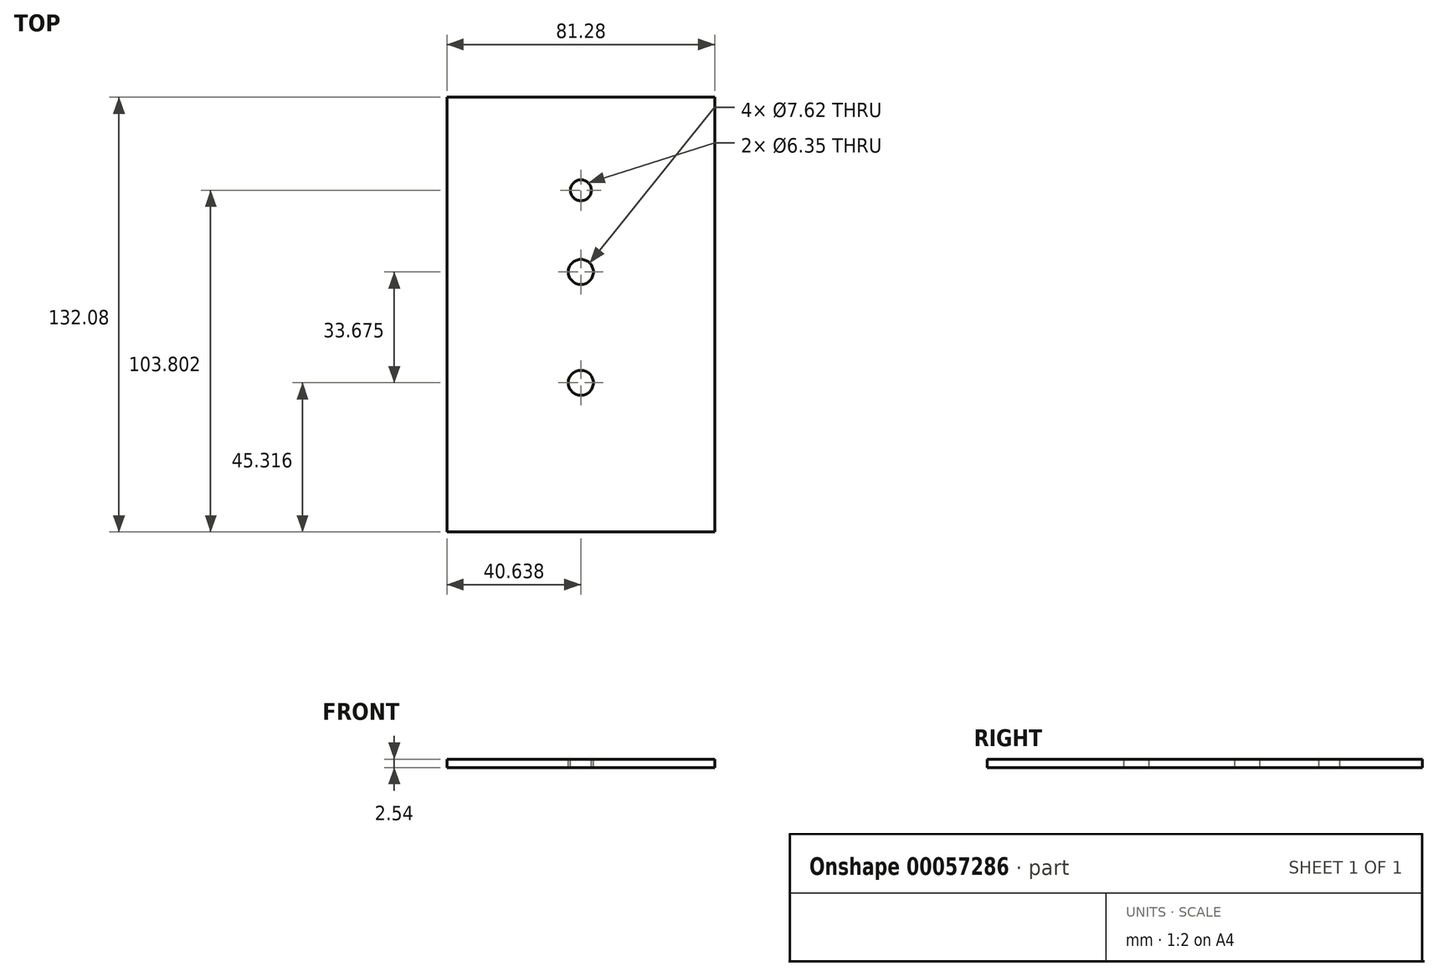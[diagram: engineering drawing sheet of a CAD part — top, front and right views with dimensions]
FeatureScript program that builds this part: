
annotation { "Feature Type Name" : "Feature", "Feature Type Description" : "" }
export const myFeature = defineFeature(function(context is Context, id is Id, definition is map)
    precondition{}
    {
        {
            var Q0;
            Q0=qCreatedBy(makeId("Top.planeOp"),FACE);
            var sketch = newSketch(context, id + "F0", { "sketchPlane" : qUnion([Q0])});
            skLineSegment(sketch, "E0.bottom", {"start": v(-159.06, -69.05) * mm, "end": v(-77.78, -69.05) * mm});
            skLineSegment(sketch, "E0.top", {"start": v(-159.06, 63.03) * mm, "end": v(-77.78, 63.03) * mm});
            skLineSegment(sketch, "E0.left", {"start": v(-159.06, -69.05) * mm, "end": v(-159.06, 63.03) * mm});
            skLineSegment(sketch, "E0.right", {"start": v(-77.78, -69.05) * mm, "end": v(-77.78, 63.03) * mm});
            skSolve(sketch);
        }
        {
            var Q0;
            Q0=makeQuery(id+"F0.imprint","IMPRINT",FACE,{"disambiguationData":[TD([[makeQuery(id+"F0.imprint","IMPRINT",EDGE,{"derivedFrom":sQuery(id+"F0.wireOp",EDGE,"E0.bottom")}),1.0]])]});
            extrude(context, id + "F1", {"entities" : qUnion([Q0]), "depth" : 2.54 * mm});
        }
        {
            var Q0;
            Q0=makeQuery(id+"F1.opExtrude","CAP_FACE",FACE,{"disambiguationData":[OSD([sQuery(id+"F0.wireOp",EDGE,"E0.bottom"),sQuery(id+"F0.wireOp",EDGE,"E0.top"),sQuery(id+"F0.wireOp",EDGE,"E0.left"),sQuery(id+"F0.wireOp",EDGE,"E0.right")])],"isStart":false});
            var sketch = newSketch(context, id + "F2", { "sketchPlane" : qUnion([Q0])});
            skCircle(sketch, "E1", {"center": v(-118.42, 34.75) * mm, "radius": 3.18 * mm});
            skSolve(sketch);
        }
        {
            var Q0;
            Q0=makeQuery(id+"F2.imprint","IMPRINT",FACE,{"disambiguationData":[TD([[makeQuery(id+"F2.imprint","IMPRINT",EDGE,{"derivedFrom":sQuery(id+"F2.wireOp",EDGE,"E1")}),-1.0]])]});
            var sketch = newSketch(context, id + "F3", { "sketchPlane" : qUnion([Q0])});
            skCircle(sketch, "E2", {"center": v(-118.42, 9.94) * mm, "radius": 3.81 * mm});
            skSolve(sketch);
        }
        {
            var Q0;
            Q0=makeQuery(id+"F2.imprint","IMPRINT",FACE,{"disambiguationData":[TD([[makeQuery(id+"F2.imprint","IMPRINT",EDGE,{"derivedFrom":sQuery(id+"F2.wireOp",EDGE,"E1")}),-1.0]])]});
            var sketch = newSketch(context, id + "F4", { "sketchPlane" : qUnion([Q0])});
            skCircle(sketch, "E3", {"center": v(-118.42, -23.73) * mm, "radius": 3.81 * mm});
            skSolve(sketch);
        }
        {
            var Q0;
            Q0 = qSketchRegion(id + "F2", true);
            extrude(context, id + "F5", {"entities" : qUnion([Q0]), "operationType" : NewBodyOperationType.REMOVE, "oppositeDirection" : true, "depth" : 2.54 * mm});
        }
        {
            var Q0;
            Q0 = qSketchRegion(id + "F4", true);
            extrude(context, id + "F6", {"entities" : qUnion([Q0]), "operationType" : NewBodyOperationType.REMOVE, "oppositeDirection" : true, "depth" : 2.54 * mm});
        }
        {
            var Q0;
            Q0 = qSketchRegion(id + "F3", true);
            extrude(context, id + "F7", {"entities" : qUnion([Q0]), "operationType" : NewBodyOperationType.REMOVE, "oppositeDirection" : true, "depth" : 2.54 * mm});
        }
    });
